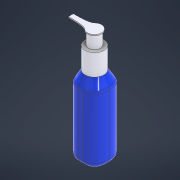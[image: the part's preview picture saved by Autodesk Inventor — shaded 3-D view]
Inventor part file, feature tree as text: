
AUTODESK INVENTOR PART (.ipt)
format: ipt  version: 2022 (Build 260153000, 153)  size: 329,728 bytes
history: native  units: in
note: dims shown in document units (in); Inventor stores cm internally (conversion verified against a paired STEP export)
features: extrude x4, sketch x4, other x4, projected_geometry x2, plane x1, loft x1, fillet x1, reference x1
ambient origin geometry x8: Origin, YZ Plane, XZ Plane, XY Plane, X Axis, Y Axis, Z Axis, Center Point
bodies: Solid1 (feature_tree)
feature tree (18):
  extrude  "Extrusion1"  Depth=1.5in
  plane  "Work Plane1"
  loft  "Loft1"
  extrude  "Extrusion2"  Depth=1.0in
  extrude  "Extrusion3"  TaperAngle=0.0deg  [1 undecoded]
  extrude  "Extrusion5"  Depth=1.125in TaperAngle=0.0deg
  fillet  "Fillet1"  Radius=0.625in
  sketch  "Sketch2"  dims[d0=1.5in d1=1.5in]
  projected_geometry  "Projected Loop1"
  other  "Edges1"
  sketch  "Sketch3"  dims[d2=0.25in d3=3.5in d4=0.0in]
  projected_geometry  "Projected Loop2"
  sketch  "Sketch4"  dims[d5=0.5in d6=1.0in]
  sketch  "Sketch5"  dims[d7=0.0in d8=90.0deg d9=0.0in d10=90.0deg d11=1.125in d12=0.0in d13=0.625in d14=0.75in d15=0.0in d16=0.75in d19=1.25in d20=0.125in d21=0.0625in d22=0.0in d23=0.25in d24=0.875in d25=0.875in]
  reference  "Reference1"
  parser-record x1  (decoder bookkeeping rows leaked as tree rows — omitted from the tree; the rows remain in map.json)
  other  "Prototype Assembly.iam"
  other  "Prototype Base:1"
note: 1 required parameter value undecoded (feature->parameter linkage not recoverable at this tier; creation-order binding heuristic only, values carry confidence <= 0.55)
note: 1 file-system path scrubbed to <path> (originals preserved in map.json)
